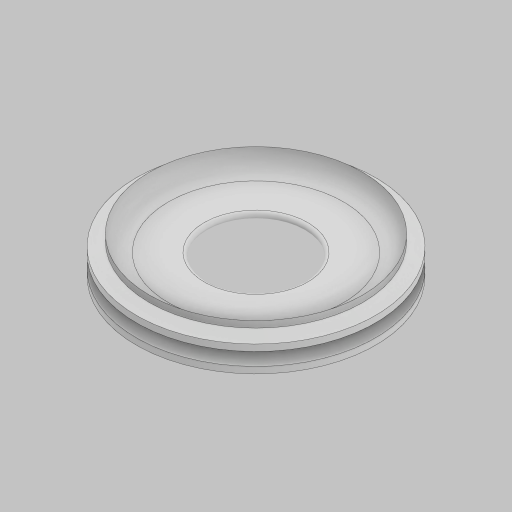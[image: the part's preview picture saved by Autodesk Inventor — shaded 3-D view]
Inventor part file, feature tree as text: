
AUTODESK INVENTOR PART (.ipt)
format: ipt  version: 2023.2 (Build 272271000, 271)  size: 184,832 bytes
history: native  units: mm
features: revolve x1, sketch x1
ambient origin geometry x8: Origin, YZ Plane, XZ Plane, XY Plane, X Axis, Y Axis, Z Axis, Center Point
bodies: Solid1 (feature_tree)
feature tree (2):
  revolve  "Revolution1"  [1 undecoded]
  sketch  "Sketch1"  dims[d3=15.0mm d4=33.0mm d5=2.0mm d7=1.0mm d8=6.0mm d9=3.0mm d10=1.0mm d12=2.0mm d13=5.54196mm d14=90.0deg d15=0.72794mm d16=12.217305mm]
note: 1 required parameter value undecoded (feature->parameter linkage not recoverable at this tier; creation-order binding heuristic only, values carry confidence <= 0.55)
